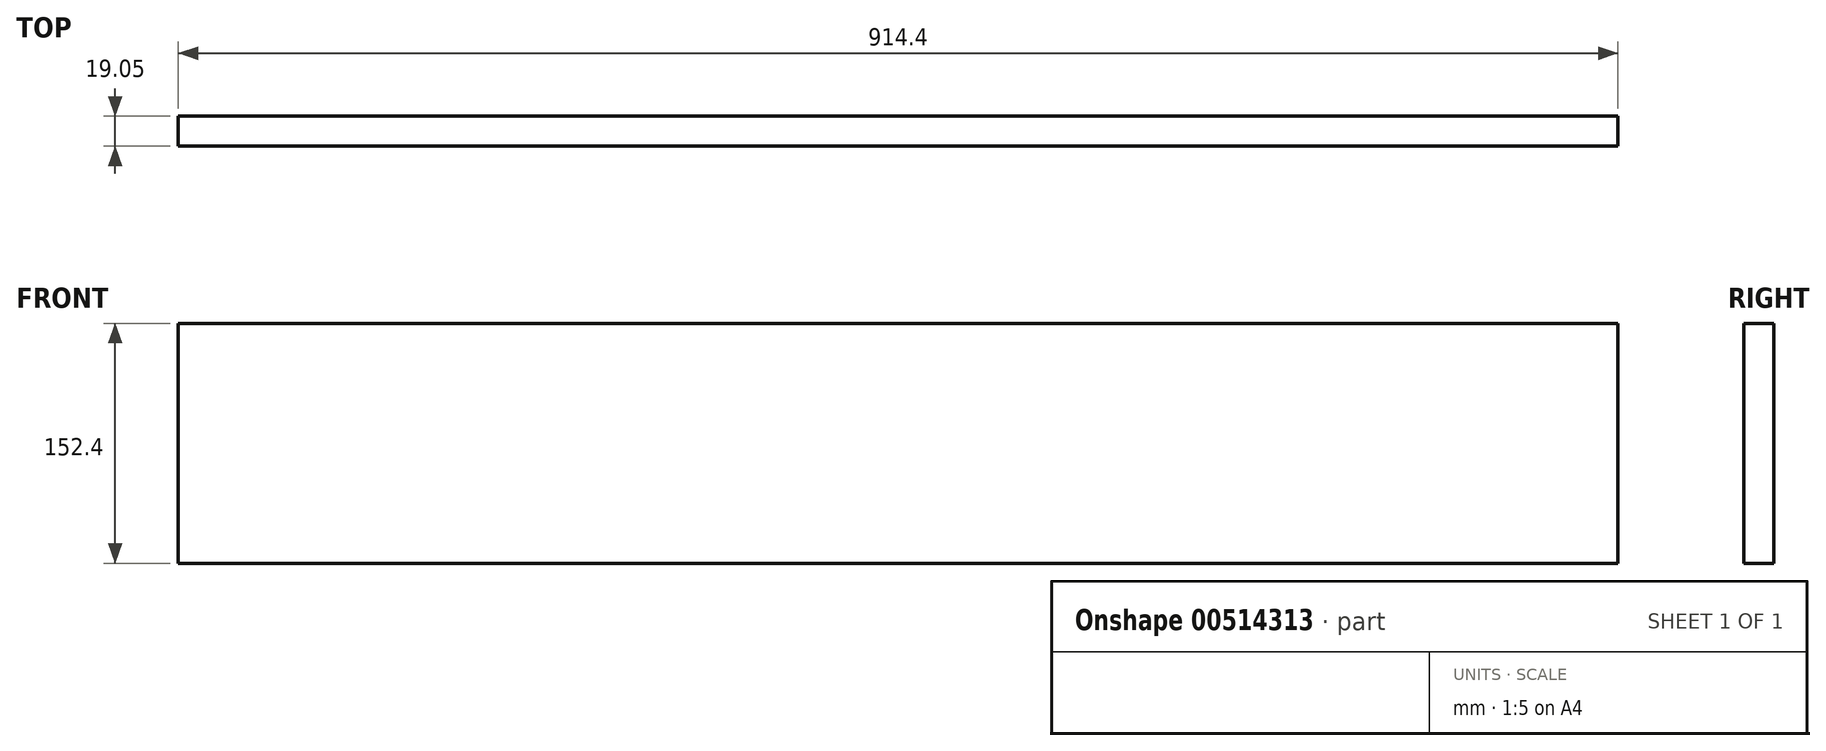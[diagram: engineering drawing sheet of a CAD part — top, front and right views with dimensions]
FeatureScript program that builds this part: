
annotation { "Feature Type Name" : "Feature", "Feature Type Description" : "" }
export const myFeature = defineFeature(function(context is Context, id is Id, definition is map)
    precondition{}
    {
        {
            var Q0;
            Q0=qCreatedBy(makeId("Front.planeOp"),FACE);
            var sketch = newSketch(context, id + "F0", { "sketchPlane" : qUnion([Q0])});
            skLineSegment(sketch, "E0.bottom", {"start": v(457.2, 352.43) * mm, "end": v(-457.2, 352.42) * mm});
            skLineSegment(sketch, "E0.top", {"start": v(457.2, -352.43) * mm, "end": v(-457.2, -352.43) * mm});
            skPoint(sketch, "E0.middle", {"position": v(0, 0) * mm});
            skLineSegment(sketch, "E1.bottom", {"start": v(-457.2, 352.42) * mm, "end": v(457.2, 352.42) * mm});
            skLineSegment(sketch, "E1.top", {"start": v(-457.2, 200.03) * mm, "end": v(457.2, 200.03) * mm});
            skLineSegment(sketch, "E1.left", {"start": v(-457.2, 352.42) * mm, "end": v(-457.2, 200.03) * mm});
            skLineSegment(sketch, "E1.right", {"start": v(457.2, 352.42) * mm, "end": v(457.2, 200.03) * mm});
            skLineSegment(sketch, "E2.top", {"start": v(457.2, -200.03) * mm, "end": v(-457.2, -200.03) * mm});
            skLineSegment(sketch, "E2.left", {"start": v(457.2, -352.43) * mm, "end": v(457.2, -200.03) * mm});
            skLineSegment(sketch, "E2.right", {"start": v(-457.2, -352.43) * mm, "end": v(-457.2, -200.03) * mm});
            skSolve(sketch);
        }
        {
            var Q0;
            Q0=makeQuery(id+"F0.imprint","IMPRINT",FACE,{"disambiguationData":[TD([[makeQuery(id+"F0.imprint","IMPRINT",EDGE,{"derivedFrom":sQuery(id+"F0.wireOp",EDGE,"E1.bottom")}),-1.0]])]});
            var Q1;
            Q1=makeQuery(id+"F0.imprint","IMPRINT",FACE,{"disambiguationData":[TD([[makeQuery(id+"F0.imprint","IMPRINT",EDGE,{"derivedFrom":sQuery(id+"F0.wireOp",EDGE,"E0.top")}),-1.0]])]});
            extrude(context, id + "F1", {"entities" : qUnion([Q0, Q1]), "depth" : 19.05 * mm});
        }
    });
